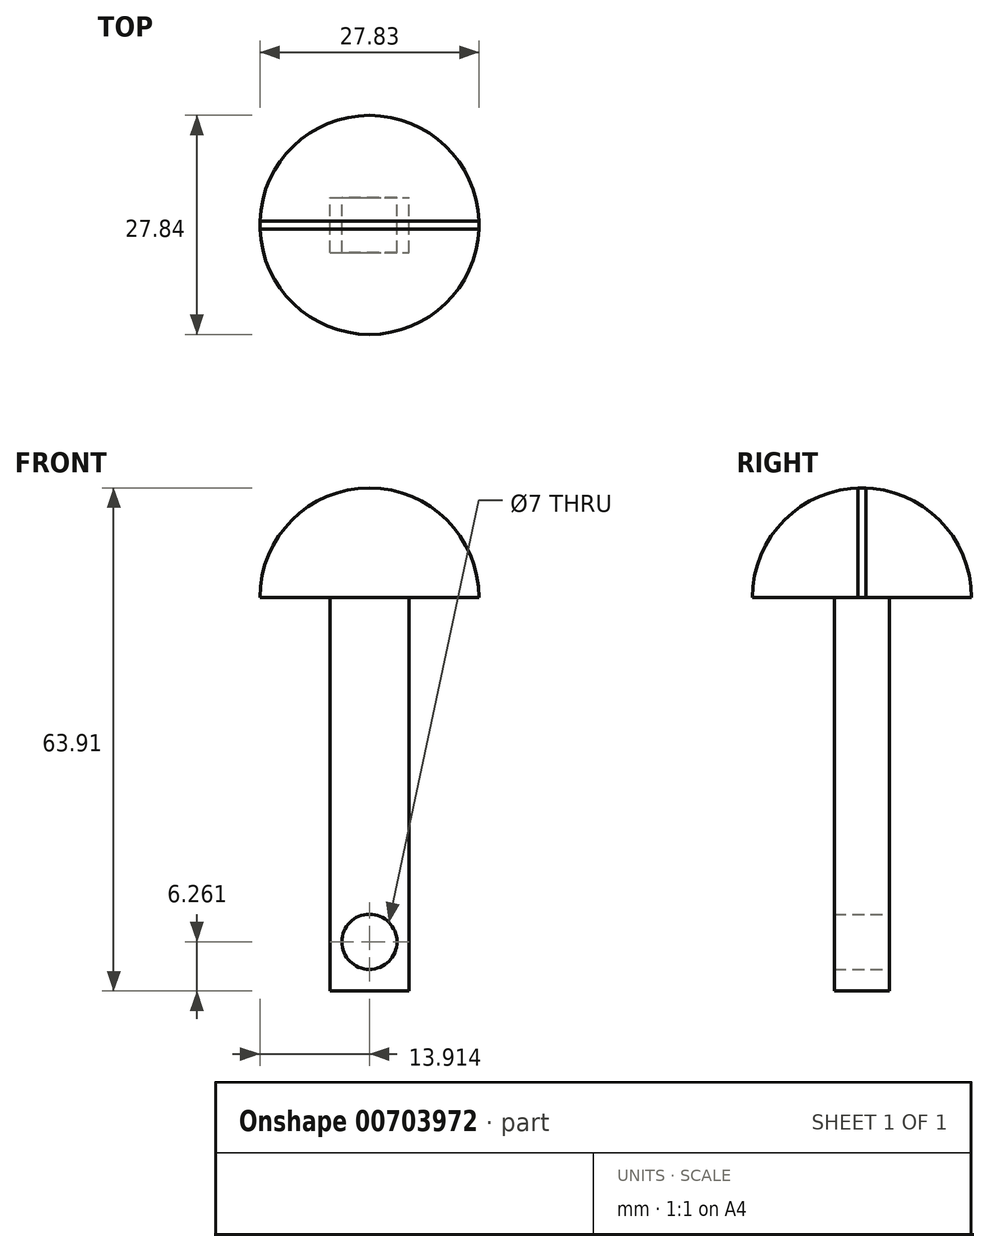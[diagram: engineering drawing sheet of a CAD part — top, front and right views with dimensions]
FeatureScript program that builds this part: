
annotation { "Feature Type Name" : "Feature", "Feature Type Description" : "" }
export const myFeature = defineFeature(function(context is Context, id is Id, definition is map)
    precondition{}
    {
        {
            var Q0;
            Q0=qCreatedBy(makeId("Front.planeOp"),FACE);
            var sketch = newSketch(context, id + "F0", { "sketchPlane" : qUnion([Q0])});
            skLineSegment(sketch, "E0.bottom", {"start": v(-14.45, 3.46) * mm, "end": v(-4.45, 3.46) * mm});
            skLineSegment(sketch, "E0.top", {"start": v(-14.45, -46.54) * mm, "end": v(-4.45, -46.54) * mm});
            skLineSegment(sketch, "E0.left", {"start": v(-14.45, 3.46) * mm, "end": v(-14.45, -46.54) * mm});
            skLineSegment(sketch, "E0.right", {"start": v(-4.45, 3.46) * mm, "end": v(-4.45, -46.54) * mm});
            skCircle(sketch, "E1", {"center": v(-9.45, -40.28) * mm, "radius": 3.5 * mm});
            skPoint(sketch, "E1.centerSnap0", {"position": v(-9.45, -46.54) * mm});
            skCircle(sketch, "E2", {"center": v(-9.45, 3.46) * mm, "radius": 13.92 * mm});
            skLineSegment(sketch, "E3", {"start": v(23.53, 3.46) * mm, "end": v(-50.85, 3.46) * mm});
            skSolve(sketch);
        }
        {
            var Q0;
            {var subQ1=sQuery(id+"F0.wireOp",EDGE,"E0.top");Q0=makeQuery(id+"F0.imprint","IMPRINT",FACE,{"disambiguationData":[TD([[makeQuery(id+"F0.imprint","IMPRINT",EDGE,{"derivedFrom":subQ1}),1.0]])]});}
            var Q1;
            {var subQ0=sQuery(id+"F0.wireOp",EDGE,"E0.bottom");Q1=makeQuery(id+"F0.imprint","IMPRINT",FACE,{"disambiguationData":[TD([[makeQuery(id+"F0.imprint","IMPRINT",EDGE,{"derivedFrom":subQ0}),-1.0]])]});}
            extrude(context, id + "F1", {"entities" : qUnion([Q0, Q1]), "endBound" : BoundingType.SYMMETRIC, "depth" : 7 * mm, "offsetDistance" : 25 * mm});
        }
        {
            var Q0;
            {var subQ0=sQuery(id+"F0.wireOp",EDGE,"E0.bottom");Q0=makeQuery(id+"F0.imprint","IMPRINT",FACE,{"disambiguationData":[TD([[makeQuery(id+"F0.imprint","IMPRINT",EDGE,{"derivedFrom":subQ0}),1.0]])]});}
            var Q1;
            Q1=sQuery(id+"F0.wireOp",EDGE,"E3");
            revolve(context, id + "F2", {"operationType" : NewBodyOperationType.ADD, "surfaceOperationType" : NewSurfaceOperationType.NEW, "entities" : qUnion([Q0]), "axis" : qUnion([Q1]), "revolveType" : RevolveType.TWO_DIRECTIONS, "angle" : 90 * degree, "angleBack" : 270 * degree});
        }
        {
            var Q0;
            {var subQ0=sQuery(id+"F0.wireOp",EDGE,"E0.bottom");Q0=makeQuery(id+"F0.imprint","IMPRINT",FACE,{"disambiguationData":[TD([[makeQuery(id+"F0.imprint","IMPRINT",EDGE,{"derivedFrom":subQ0}),1.0]])]});}
            extrude(context, id + "F3", {"entities" : qUnion([Q0]), "endBound" : BoundingType.SYMMETRIC, "depth" : 1 * mm, "offsetDistance" : 25 * mm});
        }
    });
